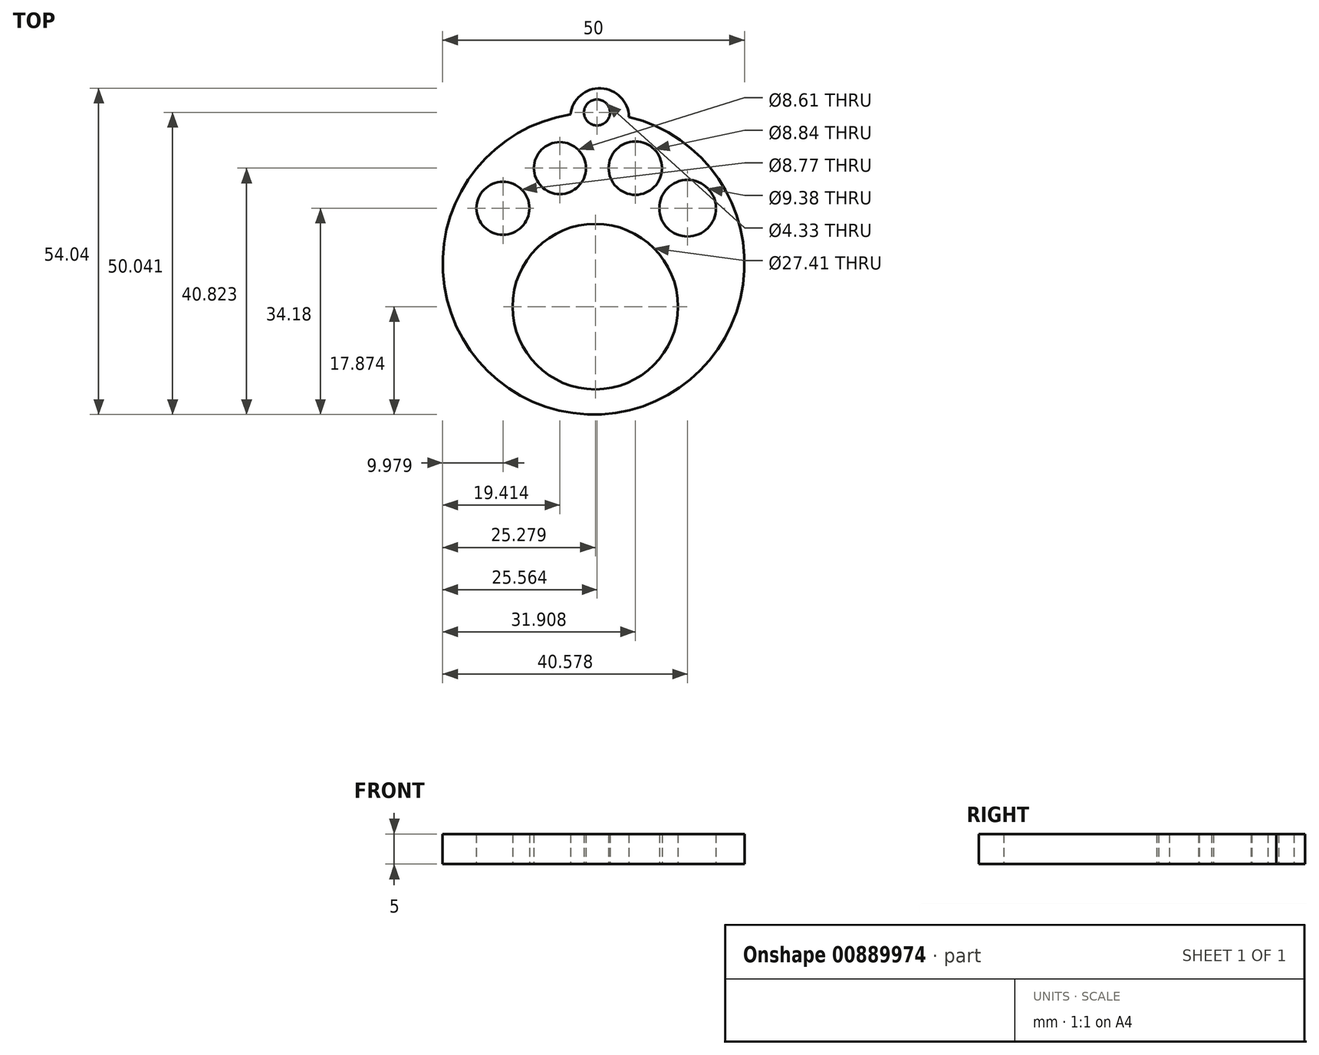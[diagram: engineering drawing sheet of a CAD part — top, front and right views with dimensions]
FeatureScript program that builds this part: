
annotation { "Feature Type Name" : "Feature", "Feature Type Description" : "" }
export const myFeature = defineFeature(function(context is Context, id is Id, definition is map)
    precondition{}
    {
        {
            var Q0;
            Q0=qCreatedBy(makeId("Top.planeOp"),FACE);
            var sketch = newSketch(context, id + "F0", { "sketchPlane" : qUnion([Q0])});
            skCircle(sketch, "E0", {"center": v(-17.77, -9.18) * mm, "radius": 25 * mm});
            skCircle(sketch, "E1", {"center": v(-17.2, 15.86) * mm, "radius": 2.16 * mm});
            skLineSegment(sketch, "E2", {"start": v(0, 0.13) * mm, "end": v(0, 0) * mm});
            skCircle(sketch, "E3", {"center": v(-17.5, -16.3) * mm, "radius": 13.7 * mm});
            skCircle(sketch, "E4", {"center": v(-23.36, 6.64) * mm, "radius": 4.3 * mm});
            skCircle(sketch, "E5", {"center": v(-10.86, 6.64) * mm, "radius": 4.42 * mm});
            skCircle(sketch, "E6", {"center": v(-32.8, 0) * mm, "radius": 4.39 * mm});
            skArc(sketch, "E7", {"start": v(-11.9, 15.13) * mm, "mid": v(-16.56, 19.86) * mm, "end": v(-21.6, 15.53) * mm});
            skCircle(sketch, "E8", {"center": v(-2.2, 0) * mm, "radius": 4.7 * mm});
            skSolve(sketch);
        }
        {
            var Q0;
            Q0 = qSketchRegion(id + "F0", true);
            var Q1;
            Q1=makeQuery(id+"F0.imprint","IMPRINT",FACE,{"disambiguationData":[TD([[makeQuery(id+"F0.imprint","IMPRINT",EDGE,{"derivedFrom":sQuery(id+"F0.wireOp",EDGE,"e5308ea1-555e-4661-aac9-915767ac85ed.sketch_text.stroke-0")}),-1.0]])]});
            var Q2;
            {var subQ0=sQuery(id+"F0.wireOp",EDGE,"e5d2ec96-d3ee-4dbc-9d47-b1b37b2a15d8.sketch_text.stroke-4");Q2=makeQuery(id+"F0.imprint","IMPRINT",FACE,{"disambiguationData":[TD([[makeQuery(id+"F0.imprint","IMPRINT",EDGE,{"derivedFrom":subQ0}),-1.0]])]});}
            extrude(context, id + "F1", {"entities" : qUnion([Q0, Q1, Q2]), "depth" : 5 * mm, "offsetDistance" : 25.4 * mm});
        }
    });
